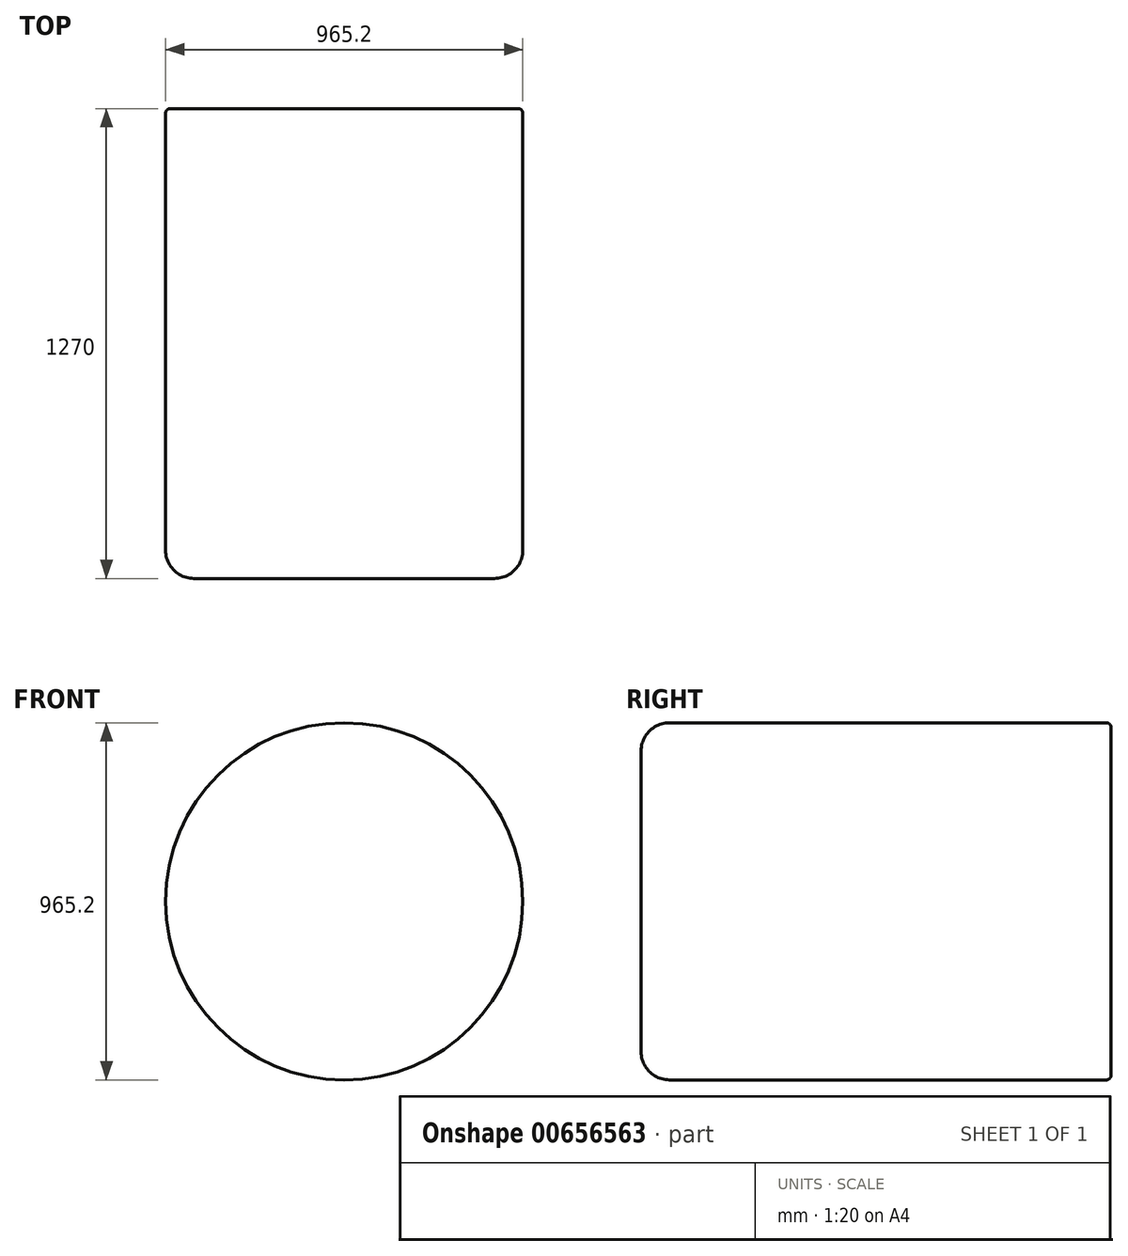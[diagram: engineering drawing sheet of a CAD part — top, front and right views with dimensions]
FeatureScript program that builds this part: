
annotation { "Feature Type Name" : "Feature", "Feature Type Description" : "" }
export const myFeature = defineFeature(function(context is Context, id is Id, definition is map)
    precondition{}
    {
        {
            var Q0;
            Q0=qCreatedBy(makeId("Front.planeOp"),FACE);
            var sketch = newSketch(context, id + "F0", { "sketchPlane" : qUnion([Q0])});
            skCircle(sketch, "E0", {"center": v(0, 0) * mm, "radius": 482.6 * mm});
            skSolve(sketch);
        }
        {
            var Q0;
            Q0=makeQuery(id+"F0.imprint","IMPRINT",FACE,{"disambiguationData":[TD([[makeQuery(id+"F0.imprint","IMPRINT",EDGE,{"derivedFrom":sQuery(id+"F0.wireOp",EDGE,"E0")}),1.0]])]});
            extrude(context, id + "F1", {"entities" : qUnion([Q0]), "depth" : 1270 * mm, "offsetDistance" : 25.4 * mm});
        }
        {
            var Q0;
            Q0=makeQuery(id+"F1.opExtrude","CAP_EDGE",EDGE,{"disambiguationData":[OSD([sQuery(id+"F0.wireOp",EDGE,"E0")])],"isStart":true});
            fillet(context, id + "F2", {"entities" : qUnion([Q0]), "radius" : 12.7 * mm, "tangentPropagation" : true, "allowEdgeOverflow" : false});
        }
        {
            var Q0;
            Q0=makeQuery(id+"F1.opExtrude","CAP_EDGE",EDGE,{"disambiguationData":[OSD([sQuery(id+"F0.wireOp",EDGE,"E0")])],"isStart":false});
            fillet(context, id + "F3", {"entities" : qUnion([Q0]), "radius" : 76.2 * mm, "tangentPropagation" : true, "allowEdgeOverflow" : false});
        }
    });
